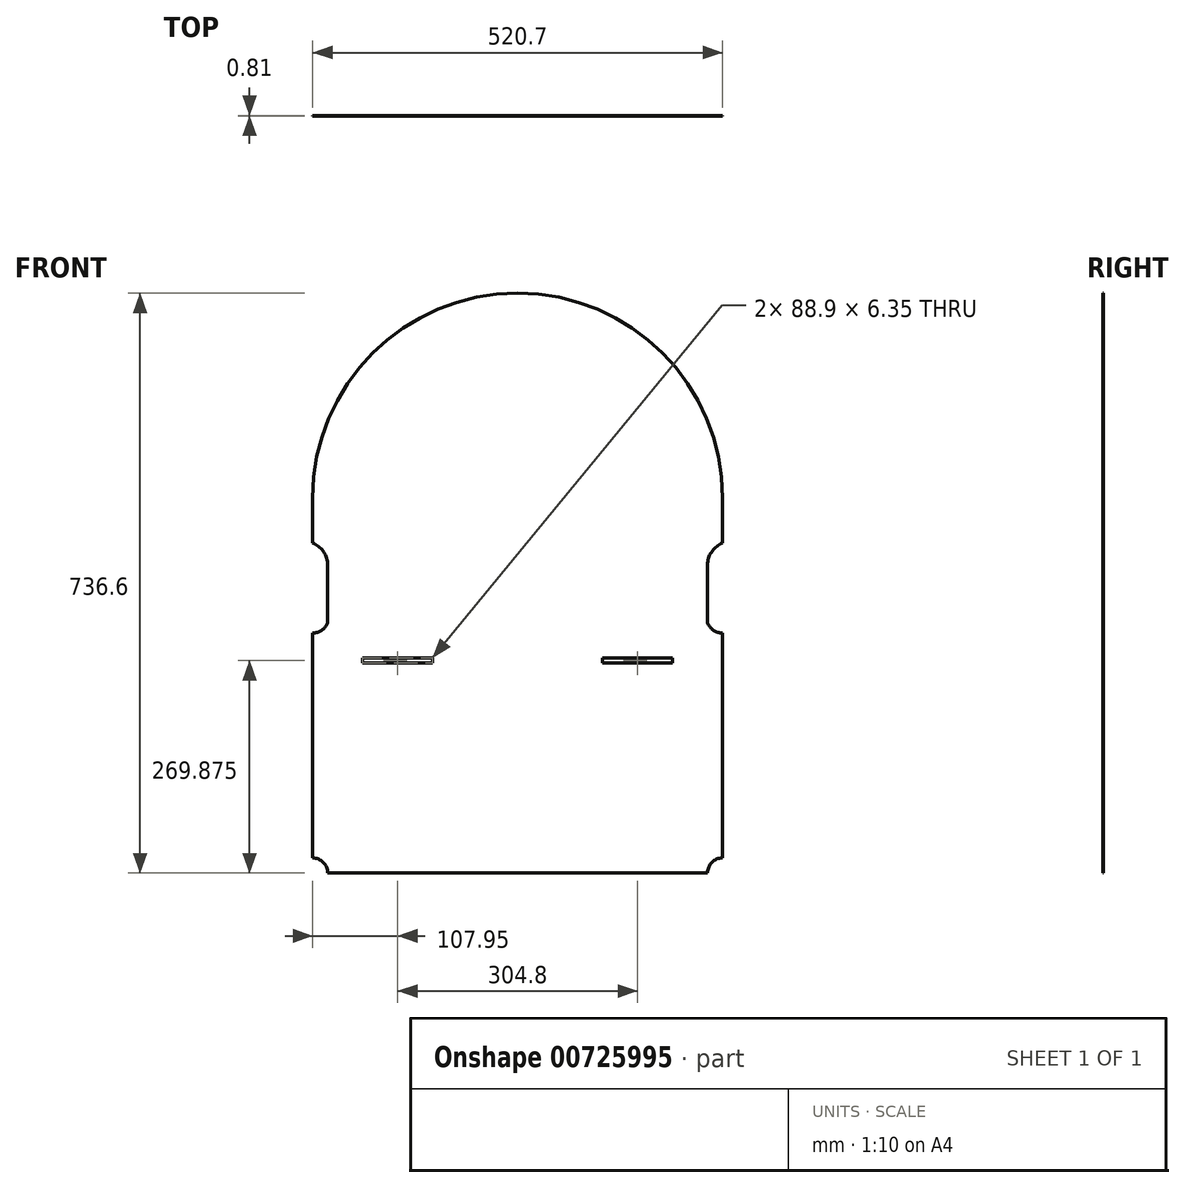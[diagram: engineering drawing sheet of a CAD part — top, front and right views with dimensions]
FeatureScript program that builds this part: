
annotation { "Feature Type Name" : "Feature", "Feature Type Description" : "" }
export const myFeature = defineFeature(function(context is Context, id is Id, definition is map)
    precondition{}
    {
        {
            var Q0;
            Q0=qCreatedBy(makeId("Front.planeOp"),FACE);
            var sketch = newSketch(context, id + "F0", { "sketchPlane" : qUnion([Q0])});
            skLineSegment(sketch, "E0.left", {"start": v(-260.35, -12.7) * mm, "end": v(-260.35, -298.45) * mm});
            skLineSegment(sketch, "E1.right", {"start": v(-241.3, 76.2) * mm, "end": v(-241.3, 0) * mm});
            skArc(sketch, "E2", {"start": v(-241.3, 76.2) * mm, "mid": v(-247.22, 91.6) * mm, "end": v(-260.35, 101.6) * mm});
            skArc(sketch, "E3", {"start": v(-260.35, -12.7) * mm, "mid": v(-248.9, -9.23) * mm, "end": v(-241.3, 0) * mm});
            skPoint(sketch, "E1.top.end.orphan", {"position": v(-241.3, -12.7) * mm});
            skArc(sketch, "E4", {"start": v(-241.3, -317.5) * mm, "mid": v(-246.88, -304.03) * mm, "end": v(-260.35, -298.45) * mm});
            skArc(sketch, "E5.MirrorCS", {"start": v(241.3, -317.5) * mm, "mid": v(246.88, -304.03) * mm, "end": v(260.35, -298.45) * mm});
            skLineSegment(sketch, "E6.MirrorCS", {"start": v(260.35, -12.7) * mm, "end": v(260.35, -298.45) * mm});
            skLineSegment(sketch, "E7.bottom", {"start": v(-196.85, -44.45) * mm, "end": v(-107.95, -44.45) * mm});
            skLineSegment(sketch, "E7.top", {"start": v(-196.85, -50.8) * mm, "end": v(-107.95, -50.8) * mm});
            skLineSegment(sketch, "E7.left", {"start": v(-196.85, -44.45) * mm, "end": v(-196.85, -50.8) * mm});
            skLineSegment(sketch, "E7.right", {"start": v(-107.95, -44.45) * mm, "end": v(-107.95, -50.8) * mm});
            skLineSegment(sketch, "E8.MirrorCS", {"start": v(107.95, -44.45) * mm, "end": v(107.95, -50.8) * mm});
            skLineSegment(sketch, "E9.MirrorCS", {"start": v(196.85, -44.45) * mm, "end": v(196.85, -50.8) * mm});
            skLineSegment(sketch, "E10.MirrorCS", {"start": v(196.85, -50.8) * mm, "end": v(107.95, -50.8) * mm});
            skLineSegment(sketch, "E11.MirrorCS", {"start": v(196.85, -44.45) * mm, "end": v(107.95, -44.45) * mm});
            skLineSegment(sketch, "E12", {"start": v(-260.35, 101.6) * mm, "end": v(-260.35, 158.75) * mm});
            skLineSegment(sketch, "E13.MirrorCS", {"start": v(260.35, 101.6) * mm, "end": v(260.35, 158.75) * mm});
            skArc(sketch, "E14", {"start": v(260.35, 158.75) * mm, "mid": v(0, 419.1) * mm, "end": v(-260.35, 158.75) * mm});
            skLineSegment(sketch, "E15", {"start": v(-241.3, -317.5) * mm, "end": v(241.3, -317.5) * mm});
            skPoint(sketch, "E16.MirrorCS.end.orphan", {"position": v(-222.25, 101.6) * mm});
            skPoint(sketch, "E16.MirrorCS.start.orphan", {"position": v(-241.3, 76.2) * mm});
            skPoint(sketch, "E17.MirrorCS.end.orphan", {"position": v(-241.3, 0) * mm});
            skPoint(sketch, "E17.MirrorCS.start.orphan", {"position": v(-222.25, -12.7) * mm});
            skPoint(sketch, "E18.MirrorP", {"position": v(241.3, -12.7) * mm});
            skLineSegment(sketch, "E19.MirrorCS", {"start": v(241.3, 76.2) * mm, "end": v(241.3, 0) * mm});
            skPoint(sketch, "E20.MirrorP", {"position": v(241.3, 76.2) * mm});
            skArc(sketch, "E21.MirrorCS", {"start": v(241.3, 76.2) * mm, "mid": v(247.22, 91.6) * mm, "end": v(260.35, 101.6) * mm});
            skPoint(sketch, "E22.MirrorP", {"position": v(241.3, 0) * mm});
            skArc(sketch, "E23.MirrorCS", {"start": v(260.35, -12.7) * mm, "mid": v(248.9, -9.23) * mm, "end": v(241.3, 0) * mm});
            skSolve(sketch);
        }
        {
            var Q0;
            Q0 = qSketchRegion(id + "F0", true);
            extrude(context, id + "F1", {"entities" : qUnion([Q0]), "depth" : 0.81 * mm, "offsetDistance" : 25.4 * mm});
        }
    });
